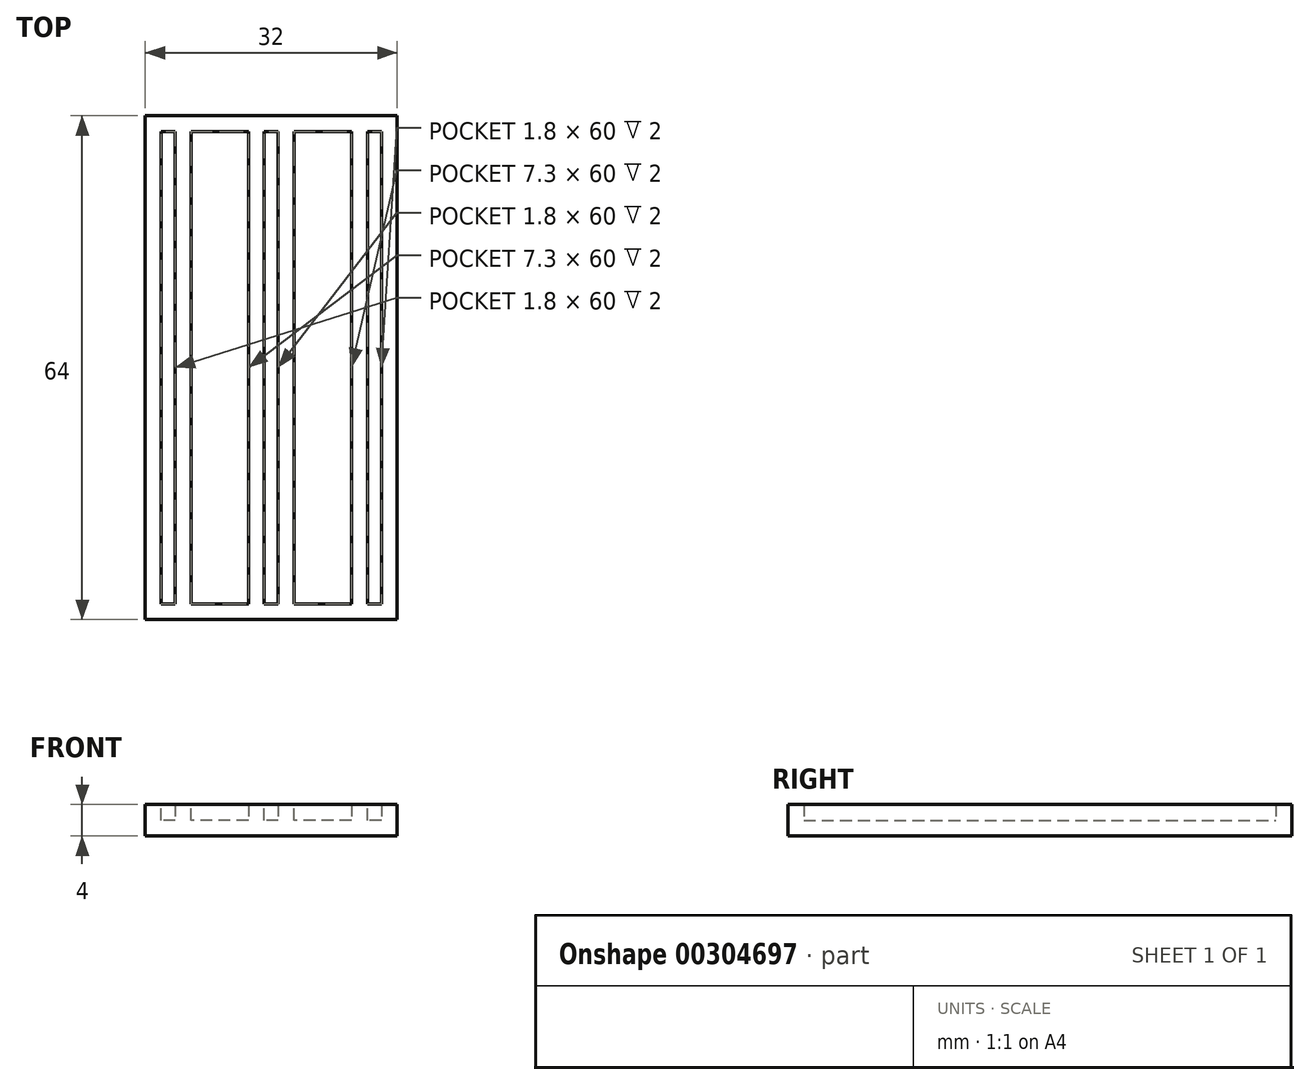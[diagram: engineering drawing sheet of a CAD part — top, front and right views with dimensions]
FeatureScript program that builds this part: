
annotation { "Feature Type Name" : "Feature", "Feature Type Description" : "" }
export const myFeature = defineFeature(function(context is Context, id is Id, definition is map)
    precondition{}
    {
        {
            var Q0;
            Q0=qCreatedBy(makeId("Front.planeOp"),FACE);
            var sketch = newSketch(context, id + "F0", { "sketchPlane" : qUnion([Q0])});
            skLineSegment(sketch, "E0", {"start": v(-16, 0) * mm, "end": v(16, 0) * mm});
            skLineSegment(sketch, "E1", {"start": v(16, 0) * mm, "end": v(16, 4) * mm});
            skLineSegment(sketch, "E2", {"start": v(16, 4) * mm, "end": v(14, 4) * mm});
            skLineSegment(sketch, "E3", {"start": v(14, 4) * mm, "end": v(14, 2) * mm});
            skLineSegment(sketch, "E4", {"start": v(14, 2) * mm, "end": v(12.2, 2) * mm});
            skLineSegment(sketch, "E5", {"start": v(12.2, 2) * mm, "end": v(12.2, 4) * mm});
            skLineSegment(sketch, "E6", {"start": v(12.2, 4) * mm, "end": v(10.2, 4) * mm});
            skLineSegment(sketch, "E7", {"start": v(10.2, 4) * mm, "end": v(10.2, 2) * mm});
            skLineSegment(sketch, "E8", {"start": v(10.2, 2) * mm, "end": v(2.9, 2) * mm});
            skLineSegment(sketch, "E9", {"start": v(2.9, 2) * mm, "end": v(2.9, 4) * mm});
            skLineSegment(sketch, "E10", {"start": v(2.9, 4) * mm, "end": v(0.9, 4) * mm});
            skLineSegment(sketch, "E11", {"start": v(0.9, 4) * mm, "end": v(0.9, 2) * mm});
            skLineSegment(sketch, "E12", {"start": v(0.9, 2) * mm, "end": v(-0.9, 2) * mm});
            skLineSegment(sketch, "E13", {"start": v(-0.9, 2) * mm, "end": v(-0.9, 4) * mm});
            skLineSegment(sketch, "E14", {"start": v(-0.9, 4) * mm, "end": v(-2.9, 4) * mm});
            skLineSegment(sketch, "E15", {"start": v(-2.9, 4) * mm, "end": v(-2.9, 2) * mm});
            skLineSegment(sketch, "E16", {"start": v(-2.9, 2) * mm, "end": v(-10.2, 2) * mm});
            skLineSegment(sketch, "E17", {"start": v(-10.2, 2) * mm, "end": v(-10.2, 4) * mm});
            skLineSegment(sketch, "E18", {"start": v(-10.2, 4) * mm, "end": v(-12.2, 4) * mm});
            skLineSegment(sketch, "E19", {"start": v(-12.2, 4) * mm, "end": v(-12.2, 2) * mm});
            skLineSegment(sketch, "E20", {"start": v(-12.2, 2) * mm, "end": v(-14, 2) * mm});
            skLineSegment(sketch, "E21", {"start": v(-14, 2) * mm, "end": v(-14, 4) * mm});
            skLineSegment(sketch, "E22", {"start": v(-14, 4) * mm, "end": v(-16, 4) * mm});
            skLineSegment(sketch, "E23", {"start": v(-16, 4) * mm, "end": v(-16, 0) * mm});
            skSolve(sketch);
        }
        {
            var Q0;
            Q0 = qSketchRegion(id + "F0", true);
            extrude(context, id + "F1", {"entities" : qUnion([Q0]), "depth" : 30 * mm, "hasSecondDirection" : true, "secondDirectionOppositeDirection" : true, "secondDirectionDepth" : 30 * mm});
        }
        {
            var Q0;
            Q0=makeQuery(id+"F1.opExtrude","CAP_FACE",FACE,{"disambiguationData":[OSD([sQuery(id+"F0.wireOp",EDGE,"E0"),sQuery(id+"F0.wireOp",EDGE,"E1"),sQuery(id+"F0.wireOp",EDGE,"E2"),sQuery(id+"F0.wireOp",EDGE,"E3"),sQuery(id+"F0.wireOp",EDGE,"E4"),sQuery(id+"F0.wireOp",EDGE,"E5"),sQuery(id+"F0.wireOp",EDGE,"E6"),sQuery(id+"F0.wireOp",EDGE,"E7"),sQuery(id+"F0.wireOp",EDGE,"E8"),sQuery(id+"F0.wireOp",EDGE,"E9"),sQuery(id+"F0.wireOp",EDGE,"E10"),sQuery(id+"F0.wireOp",EDGE,"E11"),sQuery(id+"F0.wireOp",EDGE,"E12"),sQuery(id+"F0.wireOp",EDGE,"E13"),sQuery(id+"F0.wireOp",EDGE,"E14"),sQuery(id+"F0.wireOp",EDGE,"E15"),sQuery(id+"F0.wireOp",EDGE,"E16"),sQuery(id+"F0.wireOp",EDGE,"E17"),sQuery(id+"F0.wireOp",EDGE,"E18"),sQuery(id+"F0.wireOp",EDGE,"E19"),sQuery(id+"F0.wireOp",EDGE,"E20"),sQuery(id+"F0.wireOp",EDGE,"E21"),sQuery(id+"F0.wireOp",EDGE,"E22"),sQuery(id+"F0.wireOp",EDGE,"E23")])],"isStart":false});
            var sketch = newSketch(context, id + "F2", { "sketchPlane" : qUnion([Q0])});
            skLineSegment(sketch, "E24.bottom", {"start": v(-16, 4) * mm, "end": v(16, 4) * mm});
            skLineSegment(sketch, "E24.top", {"start": v(-16, 0) * mm, "end": v(16, 0) * mm});
            skLineSegment(sketch, "E24.left", {"start": v(-16, 4) * mm, "end": v(-16, 0) * mm});
            skLineSegment(sketch, "E24.right", {"start": v(16, 4) * mm, "end": v(16, 0) * mm});
            skSolve(sketch);
        }
        {
            var Q0;
            Q0 = qSketchRegion(id + "F2", true);
            extrude(context, id + "F3", {"entities" : qUnion([Q0]), "operationType" : NewBodyOperationType.ADD, "depth" : 2 * mm});
        }
        {
            var Q0;
            Q0=makeQuery(id+"F1.opExtrude","CAP_FACE",FACE,{"disambiguationData":[OSD([sQuery(id+"F0.wireOp",EDGE,"E0"),sQuery(id+"F0.wireOp",EDGE,"E1"),sQuery(id+"F0.wireOp",EDGE,"E2"),sQuery(id+"F0.wireOp",EDGE,"E3"),sQuery(id+"F0.wireOp",EDGE,"E4"),sQuery(id+"F0.wireOp",EDGE,"E5"),sQuery(id+"F0.wireOp",EDGE,"E6"),sQuery(id+"F0.wireOp",EDGE,"E7"),sQuery(id+"F0.wireOp",EDGE,"E8"),sQuery(id+"F0.wireOp",EDGE,"E9"),sQuery(id+"F0.wireOp",EDGE,"E10"),sQuery(id+"F0.wireOp",EDGE,"E11"),sQuery(id+"F0.wireOp",EDGE,"E12"),sQuery(id+"F0.wireOp",EDGE,"E13"),sQuery(id+"F0.wireOp",EDGE,"E14"),sQuery(id+"F0.wireOp",EDGE,"E15"),sQuery(id+"F0.wireOp",EDGE,"E16"),sQuery(id+"F0.wireOp",EDGE,"E17"),sQuery(id+"F0.wireOp",EDGE,"E18"),sQuery(id+"F0.wireOp",EDGE,"E19"),sQuery(id+"F0.wireOp",EDGE,"E20"),sQuery(id+"F0.wireOp",EDGE,"E21"),sQuery(id+"F0.wireOp",EDGE,"E22"),sQuery(id+"F0.wireOp",EDGE,"E23")])],"isStart":true});
            var sketch = newSketch(context, id + "F4", { "sketchPlane" : qUnion([Q0])});
            skLineSegment(sketch, "E25.bottom", {"start": v(-16, 4) * mm, "end": v(16, 4) * mm});
            skLineSegment(sketch, "E25.top", {"start": v(-16, 0) * mm, "end": v(16, 0) * mm});
            skLineSegment(sketch, "E25.left", {"start": v(-16, 4) * mm, "end": v(-16, 0) * mm});
            skLineSegment(sketch, "E25.right", {"start": v(16, 4) * mm, "end": v(16, 0) * mm});
            skSolve(sketch);
        }
        {
            var Q0;
            Q0 = qSketchRegion(id + "F4", true);
            extrude(context, id + "F5", {"entities" : qUnion([Q0]), "operationType" : NewBodyOperationType.ADD, "depth" : 2 * mm});
        }
    });
